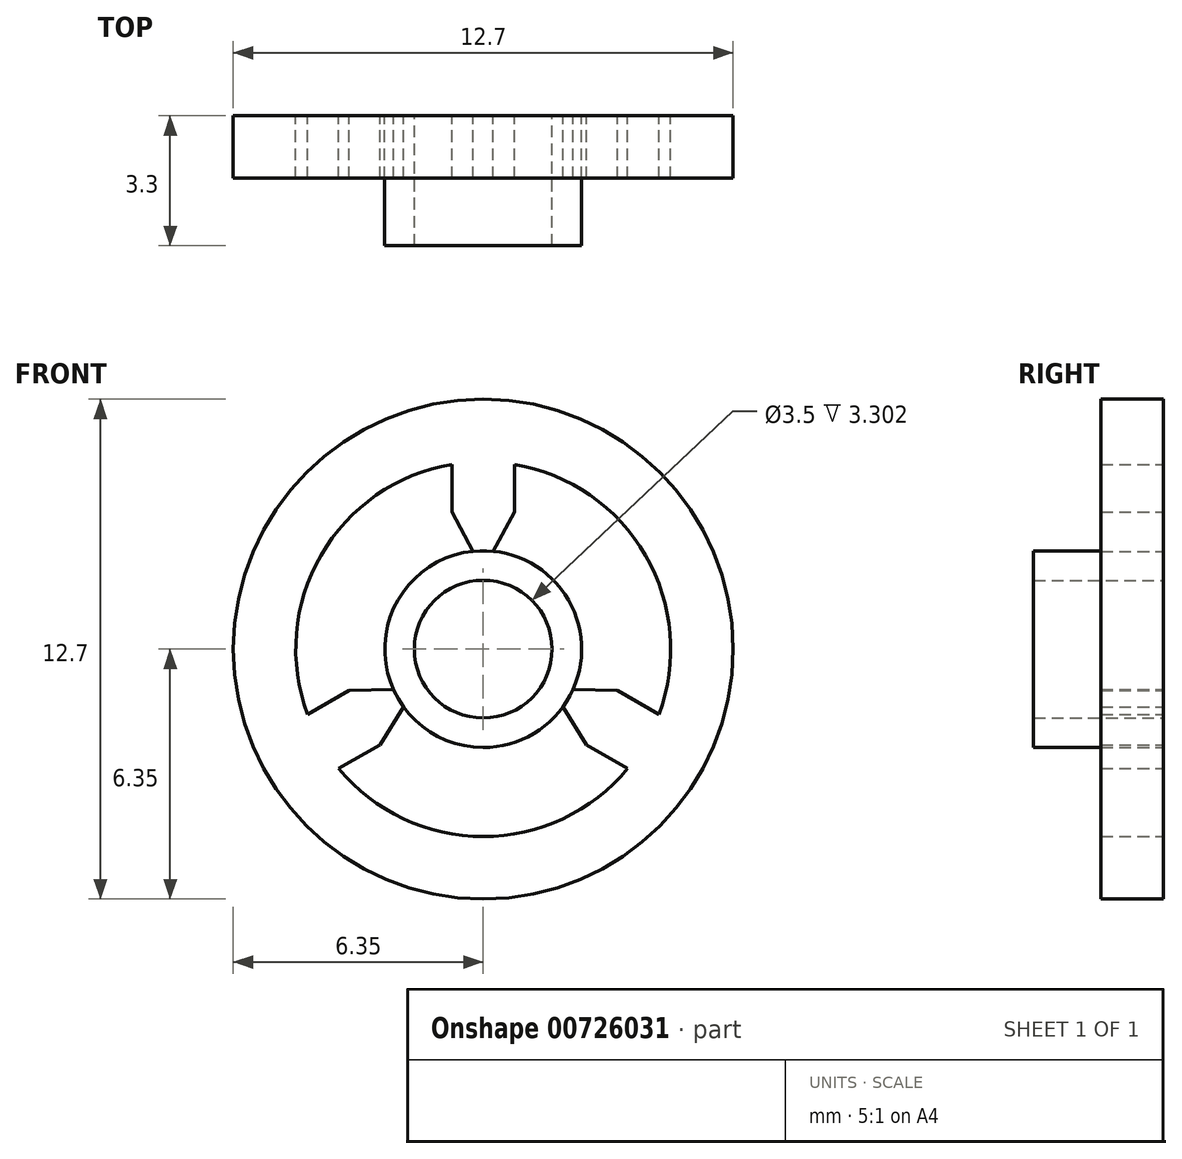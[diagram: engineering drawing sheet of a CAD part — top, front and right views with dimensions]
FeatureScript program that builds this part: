
annotation { "Feature Type Name" : "Feature", "Feature Type Description" : "" }
export const myFeature = defineFeature(function(context is Context, id is Id, definition is map)
    precondition{}
    {
        {
            var Q0;
            Q0=qCreatedBy(makeId("Front.planeOp"),FACE);
            var sketch = newSketch(context, id + "F0", { "sketchPlane" : qUnion([Q0])});
            skCircle(sketch, "E0", {"center": v(0, 0) * mm, "radius": 1.75 * mm});
            skCircle(sketch, "E1", {"center": v(0, 0) * mm, "radius": 2.5 * mm});
            skCircle(sketch, "E2", {"center": v(0, 0) * mm, "radius": 6.35 * mm});
            skCircle(sketch, "E3", {"center": v(0, 0) * mm, "radius": 4.76 * mm});
            skCircle(sketch, "E4", {"center": v(0, 0) * mm, "radius": 3.57 * mm, "construction": true});
            skLineSegment(sketch, "E5", {"start": v(-0.8, 4.7) * mm, "end": v(-0.8, 3.48) * mm});
            skLineSegment(sketch, "E6", {"start": v(-0.8, 3.48) * mm, "end": v(-0.25, 2.49) * mm});
            skLineSegment(sketch, "E7", {"start": v(0, 1.75) * mm, "end": v(0, -1.75) * mm, "construction": true});
            skLineSegment(sketch, "E8.MirrorCS", {"start": v(0.8, 4.7) * mm, "end": v(0.8, 3.48) * mm});
            skLineSegment(sketch, "E9.MirrorCS", {"start": v(0.8, 3.48) * mm, "end": v(0.25, 2.49) * mm});
            skLineSegment(sketch, "E10.1.0", {"start": v(-4.46, -1.66) * mm, "end": v(-3.41, -1.05) * mm});
            skLineSegment(sketch, "E10.1.1", {"start": v(-3.41, -1.05) * mm, "end": v(-2.28, -1.02) * mm});
            skLineSegment(sketch, "E10.1.2", {"start": v(-2.62, -2.43) * mm, "end": v(-2.03, -1.46) * mm});
            skLineSegment(sketch, "E10.1.3", {"start": v(-3.67, -3.04) * mm, "end": v(-2.62, -2.43) * mm});
            skLineSegment(sketch, "E10.2.0", {"start": v(3.67, -3.04) * mm, "end": v(2.62, -2.43) * mm});
            skLineSegment(sketch, "E10.2.1", {"start": v(2.62, -2.43) * mm, "end": v(2.03, -1.46) * mm});
            skLineSegment(sketch, "E10.2.2", {"start": v(3.41, -1.05) * mm, "end": v(2.28, -1.02) * mm});
            skLineSegment(sketch, "E10.2.3", {"start": v(4.46, -1.66) * mm, "end": v(3.41, -1.05) * mm});
            skSolve(sketch);
        }
        {
            var Q0;
            Q0=makeQuery(id+"F0.imprint","IMPRINT",FACE,{"disambiguationData":[TD([[makeQuery(id+"F0.imprint","IMPRINT",EDGE,{"derivedFrom":sQuery(id+"F0.wireOp",EDGE,"E0")}),-1.0]])]});
            extrude(context, id + "F1", {"entities" : qUnion([Q0]), "depth" : 3.3 * mm, "offsetDistance" : 25.4 * mm});
        }
        {
            var Q0;
            Q0=makeQuery(id+"F0.imprint","IMPRINT",FACE,{"disambiguationData":[TD([[makeQuery(id+"F0.imprint","IMPRINT",EDGE,{"derivedFrom":sQuery(id+"F0.wireOp",EDGE,"E2")}),1.0]])]});
            var Q1;
            {var subQ1=sQuery(id+"F0.wireOp",EDGE,"E5");Q1=makeQuery(id+"F0.imprint","IMPRINT",FACE,{"disambiguationData":[TD([[makeQuery(id+"F0.imprint","IMPRINT",EDGE,{"derivedFrom":subQ1}),1.0]])]});}
            var Q2;
            {var subQ1=sQuery(id+"F0.wireOp",EDGE,"E10.1.0");Q2=makeQuery(id+"F0.imprint","IMPRINT",FACE,{"disambiguationData":[TD([[makeQuery(id+"F0.imprint","IMPRINT",EDGE,{"derivedFrom":subQ1}),-1.0]])]});}
            var Q3;
            {var subQ1=sQuery(id+"F0.wireOp",EDGE,"E10.2.0");Q3=makeQuery(id+"F0.imprint","IMPRINT",FACE,{"disambiguationData":[TD([[makeQuery(id+"F0.imprint","IMPRINT",EDGE,{"derivedFrom":subQ1}),-1.0]])]});}
            extrude(context, id + "F2", {"entities" : qUnion([Q0, Q1, Q2, Q3]), "operationType" : NewBodyOperationType.ADD, "depth" : 1.59 * mm, "offsetDistance" : 25.4 * mm});
        }
    });
